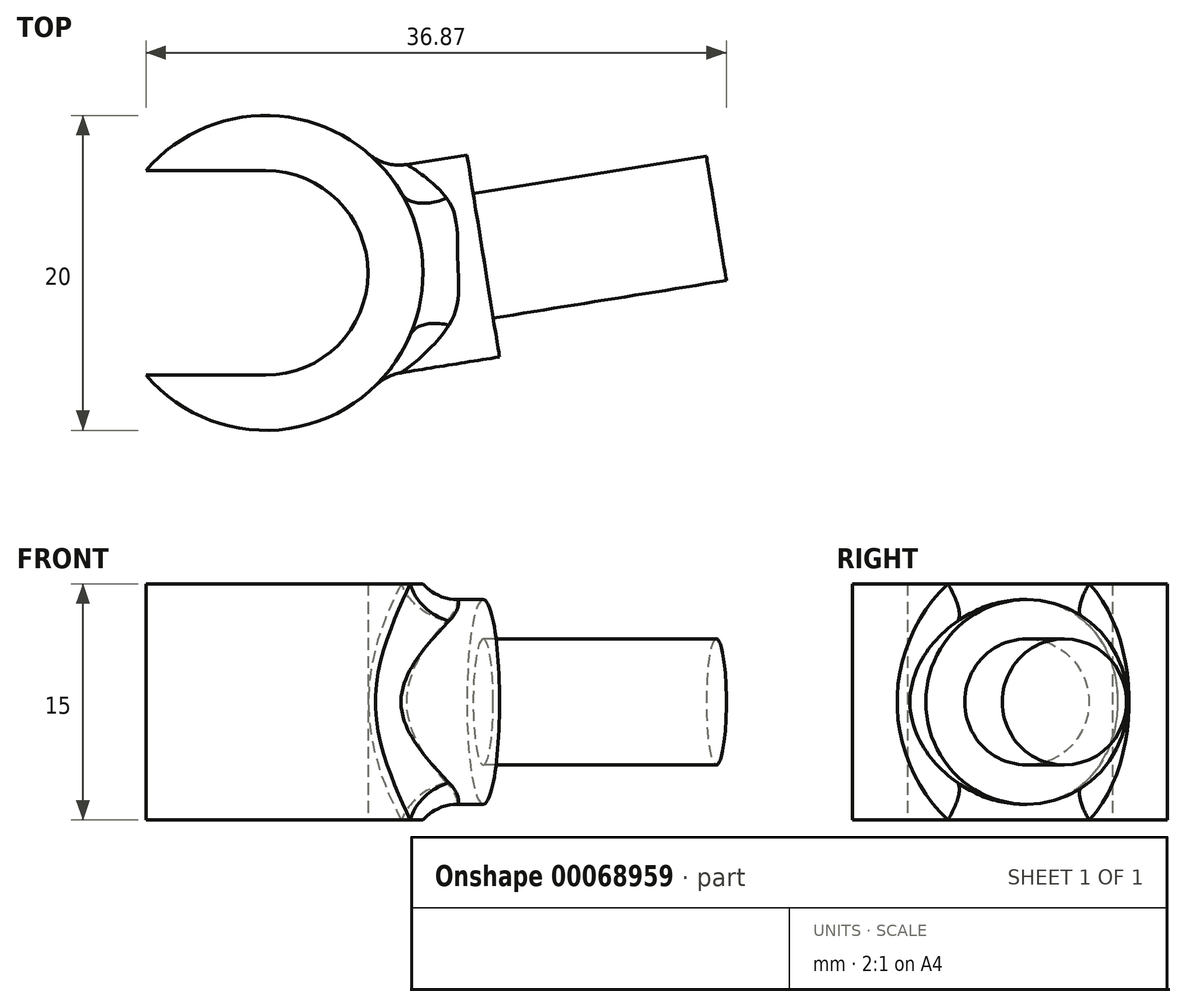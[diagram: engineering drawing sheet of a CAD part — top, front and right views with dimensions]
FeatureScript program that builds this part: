
annotation { "Feature Type Name" : "Feature", "Feature Type Description" : "" }
export const myFeature = defineFeature(function(context is Context, id is Id, definition is map)
    precondition{}
    {
        {
            var Q0;
            Q0=qCreatedBy(makeId("Top.planeOp"),FACE);
            var sketch = newSketch(context, id + "F0", { "sketchPlane" : qUnion([Q0])});
            skArc(sketch, "E0", {"start": v(-7.6, -6.5) * mm, "mid": v(10, 0) * mm, "end": v(-7.6, 6.5) * mm});
            skArc(sketch, "E1", {"start": v(0, -6.5) * mm, "mid": v(6.5, 0) * mm, "end": v(0, 6.5) * mm});
            skLineSegment(sketch, "E2", {"start": v(0, 6.5) * mm, "end": v(-7.6, 6.5) * mm});
            skLineSegment(sketch, "E3", {"start": v(0, -6.5) * mm, "end": v(-7.6, -6.5) * mm});
            skSolve(sketch);
        }
        {
            var Q0;
            Q0=makeQuery(id+"F0.imprint","IMPRINT",FACE,{"disambiguationData":[TD([[makeQuery(id+"F0.imprint","IMPRINT",EDGE,{"derivedFrom":sQuery(id+"F0.wireOp",EDGE,"E0")}),1.0]])]});
            extrude(context, id + "F1", {"entities" : qUnion([Q0]), "endBound" : BoundingType.SYMMETRIC, "depth" : 15 * mm});
        }
        {
            var Q0;
            Q0=qCreatedBy(makeId("Top.planeOp"),FACE);
            var sketch = newSketch(context, id + "F2", { "sketchPlane" : qUnion([Q0])});
            skLineSegment(sketch, "E4", {"start": v(7.1, 0) * mm, "end": v(28.63, 3.47) * mm});
            skLineSegment(sketch, "E5", {"start": v(28.63, 3.47) * mm, "end": v(29.27, -0.48) * mm});
            skLineSegment(sketch, "E6", {"start": v(29.27, -0.48) * mm, "end": v(14.46, -2.87) * mm});
            skLineSegment(sketch, "E7", {"start": v(14.46, -2.87) * mm, "end": v(14.86, -5.33) * mm});
            skLineSegment(sketch, "E8", {"start": v(14.86, -5.33) * mm, "end": v(5.48, -6.84) * mm});
            skLineSegment(sketch, "E9", {"start": v(5.48, -6.84) * mm, "end": v(7.1, 0) * mm});
            skSolve(sketch);
        }
        {
            var Q0;
            Q0=makeQuery(id+"F2.imprint","IMPRINT",FACE,{"disambiguationData":[TD([[makeQuery(id+"F2.imprint","IMPRINT",EDGE,{"derivedFrom":sQuery(id+"F2.wireOp",EDGE,"E4")}),-1.0]])]});
            var Q1;
            Q1=sQuery(id+"F2.wireOp",EDGE,"E4");
            revolve(context, id + "F3", {"operationType" : NewBodyOperationType.ADD, "entities" : qUnion([Q0]), "axis" : qUnion([Q1]), "revolveType" : RevolveType.FULL});
        }
        {
            var Q0;
            Q0=qCreatedBy(makeId("Top.planeOp"),FACE);
            var sketch = newSketch(context, id + "F4", { "sketchPlane" : qUnion([Q0])});
            skCircle(sketch, "E10", {"center": v(0, 0) * mm, "radius": 6.5 * mm});
            skSolve(sketch);
        }
        {
            var Q0;
            Q0 = qSketchRegion(id + "F4", true);
            extrude(context, id + "F5", {"entities" : qUnion([Q0]), "operationType" : NewBodyOperationType.REMOVE, "endBound" : BoundingType.SYMMETRIC, "oppositeDirection" : true, "depth" : 25 * mm});
        }
        {
            var Q0;
            Q0=makeQuery(id+"F3.boolean.opBoolean","INTERSECT",EDGE,{"derivedFrom":[makeQuery(id+"F1.opExtrude","SWEPT_FACE",FACE,{"disambiguationData":[OSD([sQuery(id+"F0.wireOp",EDGE,"E0")])]}),makeQuery(id+"F3.opRevolve","SWEPT_FACE",FACE,{"disambiguationData":[OSD([sQuery(id+"F2.wireOp",EDGE,"E8")])]})]});
            fillet(context, id + "F6", {"entities" : qUnion([Q0]), "radius" : 3 * mm, "allowEdgeOverflow" : false});
        }
    });
